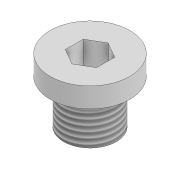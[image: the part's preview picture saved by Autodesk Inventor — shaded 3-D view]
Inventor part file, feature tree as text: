
AUTODESK INVENTOR PART (.ipt)
format: ipt  version: 2022.3 (Build 263350000, 350)  size: 116,736 bytes
history: native  units: mm
features: extrude x4, sketch x4, other x1, thread x1
ambient origin geometry x8: Origin, YZ Plane, XZ Plane, XY Plane, X Axis, Y Axis, Z Axis, Center Point
bodies: Body1 (feature_tree)
feature tree (10):
  other  "Sólido1"
  extrude  "Extrusión1"  Depth=12.0mm TaperAngle=0.0deg
  extrude  "Extrusión2"  Depth=5.5mm TaperAngle=0.0deg
  extrude  "Extrusión3"  Depth=11.4mm TaperAngle=0.0deg
  thread  "Rosca1"  [1 undecoded]
  extrude  "Extrusión4"  Depth=1.0mm TaperAngle=0.0deg
  sketch  "Boceto1"  dims[d0=14.55mm d1=12.0mm d2=0.0mm]
  sketch  "Boceto2"  dims[d3=22.0mm d4=5.5mm d5=0.0mm]
  sketch  "Boceto3"  dims[d6=4.325mm d7=11.4mm d8=0.0mm d9=9.0mm d10=0.0mm]
  sketch  "Boceto4"  dims[d11=20.0mm d12=1.0mm d13=0.0mm]
note: 1 required parameter value undecoded (feature->parameter linkage not recoverable at this tier; creation-order binding heuristic only, values carry confidence <= 0.55)
